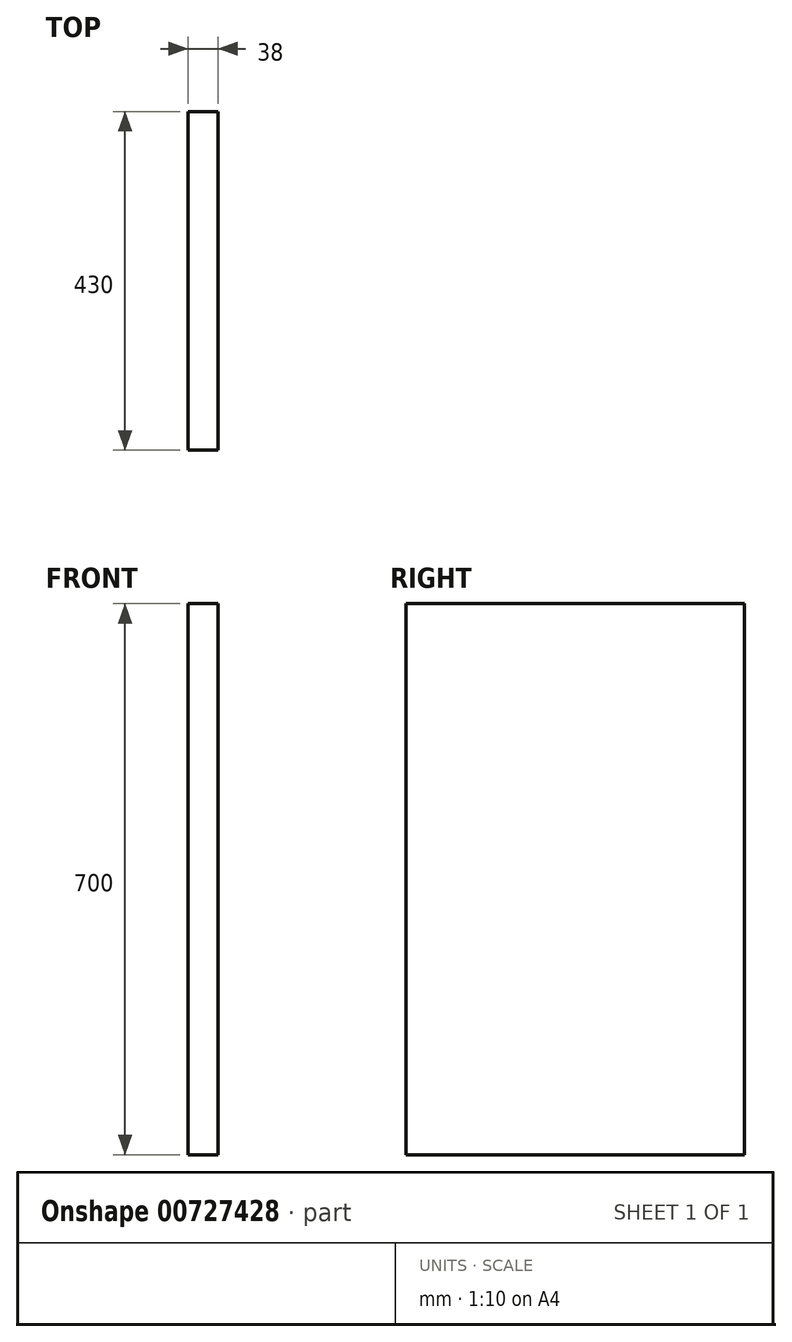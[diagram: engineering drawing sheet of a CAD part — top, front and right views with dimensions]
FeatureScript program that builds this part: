
annotation { "Feature Type Name" : "Feature", "Feature Type Description" : "" }
export const myFeature = defineFeature(function(context is Context, id is Id, definition is map)
    precondition{}
    {
        {
            var Q0;
            Q0=qCreatedBy(makeId("Right.planeOp"),FACE);
            var sketch = newSketch(context, id + "F0", { "sketchPlane" : qUnion([Q0])});
            skLineSegment(sketch, "E0.bottom", {"start": v(219.14, 483.73) * mm, "end": v(-210.86, 483.73) * mm});
            skLineSegment(sketch, "E0.top", {"start": v(219.14, -216.27) * mm, "end": v(-210.86, -216.27) * mm});
            skLineSegment(sketch, "E0.left", {"start": v(219.14, 483.73) * mm, "end": v(219.14, -216.27) * mm});
            skLineSegment(sketch, "E0.right", {"start": v(-210.86, 483.73) * mm, "end": v(-210.86, -216.27) * mm});
            skSolve(sketch);
        }
        {
            var Q0;
            Q0 = qSketchRegion(id + "F0", true);
            extrude(context, id + "F1", {"entities" : qUnion([Q0]), "depth" : 38 * mm, "offsetDistance" : 25 * mm});
        }
    });
